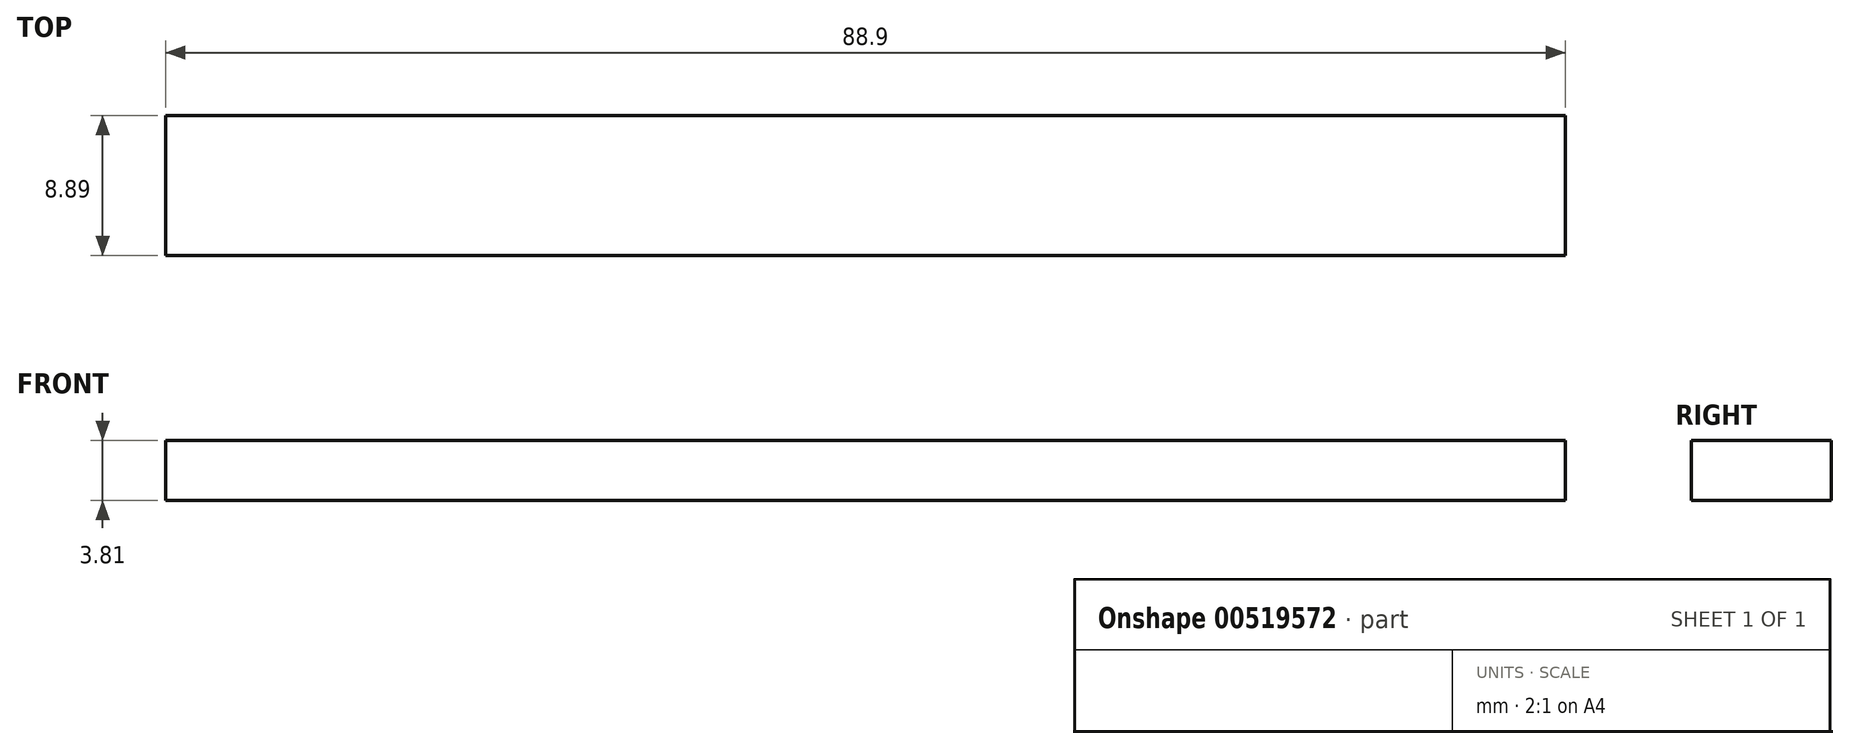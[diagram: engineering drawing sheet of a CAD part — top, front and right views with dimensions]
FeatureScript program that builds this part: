
annotation { "Feature Type Name" : "Feature", "Feature Type Description" : "" }
export const myFeature = defineFeature(function(context is Context, id is Id, definition is map)
    precondition{}
    {
        {
            var Q0;
            Q0=qCreatedBy(makeId("Top.planeOp"),FACE);
            var sketch = newSketch(context, id + "F0", { "sketchPlane" : qUnion([Q0])});
            skLineSegment(sketch, "E0.bottom", {"start": v(-39.2, 36.73) * mm, "end": v(49.7, 36.73) * mm});
            skLineSegment(sketch, "E0.top", {"start": v(-39.2, 27.84) * mm, "end": v(49.7, 27.84) * mm});
            skLineSegment(sketch, "E0.left", {"start": v(-39.2, 36.73) * mm, "end": v(-39.2, 27.84) * mm});
            skLineSegment(sketch, "E0.right", {"start": v(49.7, 36.73) * mm, "end": v(49.7, 27.84) * mm});
            skSolve(sketch);
        }
        {
            var Q0;
            Q0 = qSketchRegion(id + "F0", true);
            extrude(context, id + "F1", {"entities" : qUnion([Q0]), "depth" : 3.8 * mm, "offsetDistance" : 25.4 * mm});
        }
    });
